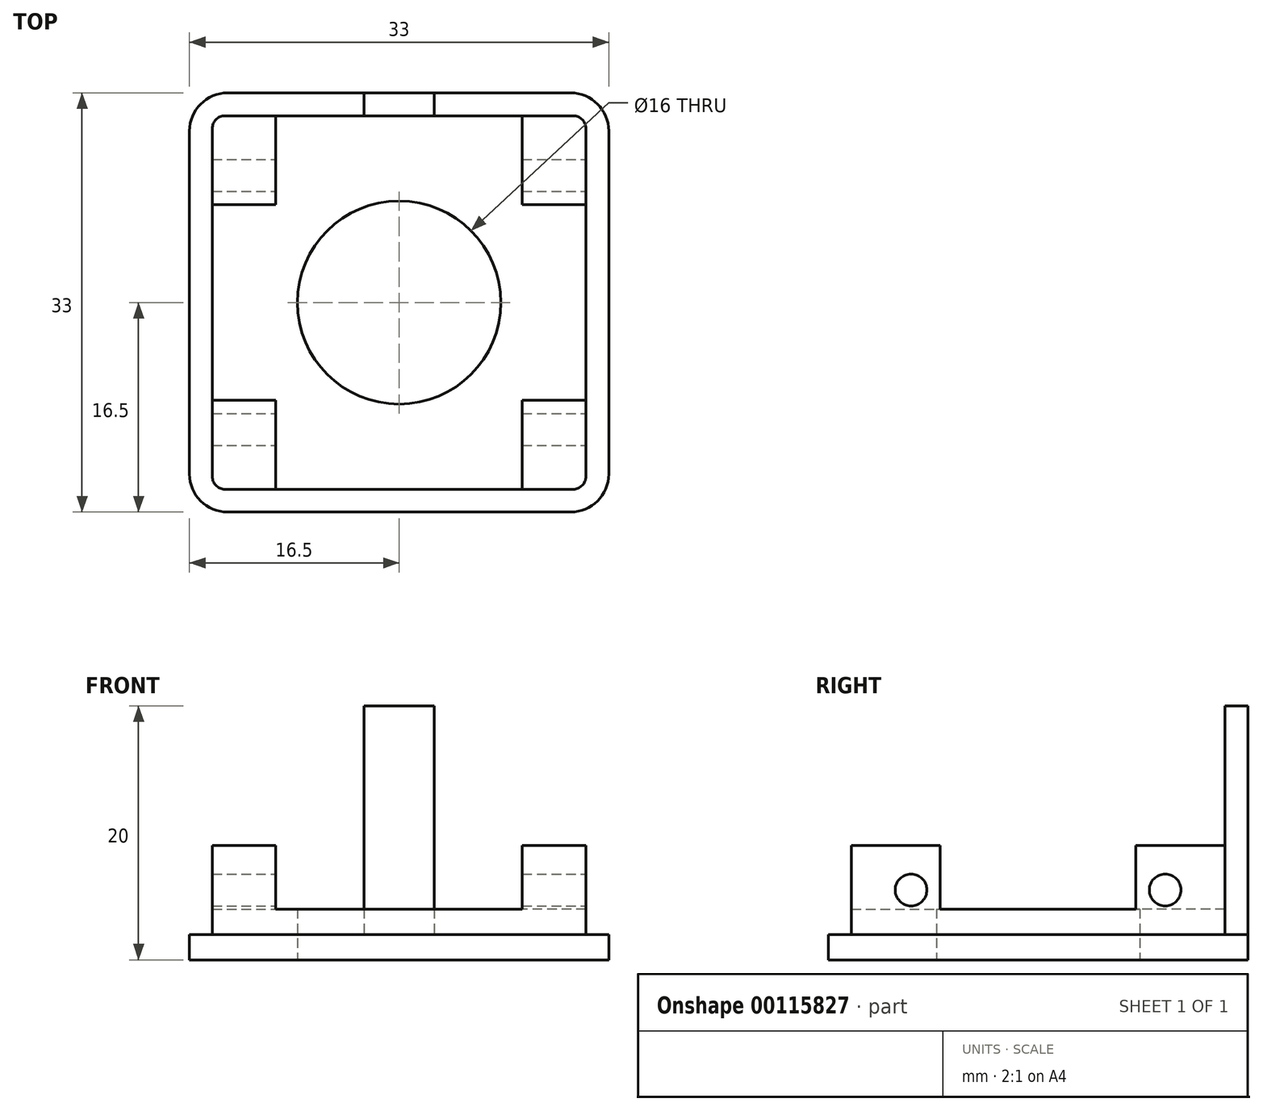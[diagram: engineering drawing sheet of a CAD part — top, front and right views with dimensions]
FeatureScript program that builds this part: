
annotation { "Feature Type Name" : "Feature", "Feature Type Description" : "" }
export const myFeature = defineFeature(function(context is Context, id is Id, definition is map)
    precondition{}
    {
        {
            var Q0;
            Q0=qCreatedBy(makeId("Top.planeOp"),FACE);
            var sketch = newSketch(context, id + "F0", { "sketchPlane" : qUnion([Q0])});
            skLineSegment(sketch, "E0.bottom", {"start": v(0, 0) * mm, "end": v(33, 0) * mm});
            skLineSegment(sketch, "E0.top", {"start": v(0, -33) * mm, "end": v(33, -33) * mm});
            skLineSegment(sketch, "E0.left", {"start": v(0, 0) * mm, "end": v(0, -33) * mm});
            skLineSegment(sketch, "E0.right", {"start": v(33, 0) * mm, "end": v(33, -33) * mm});
            skSolve(sketch);
        }
        {
            var Q0;
            Q0 = qSketchRegion(id + "F0", true);
            extrude(context, id + "F1", {"entities" : qUnion([Q0]), "depth" : 2 * mm});
        }
        {
            var Q0;
            Q0=makeQuery(id+"F1.opExtrude","CAP_FACE",FACE,{"disambiguationData":[OSD([sQuery(id+"F0.wireOp",EDGE,"E0.bottom"),sQuery(id+"F0.wireOp",EDGE,"E0.top"),sQuery(id+"F0.wireOp",EDGE,"E0.left"),sQuery(id+"F0.wireOp",EDGE,"E0.right")])],"isStart":false});
            var sketch = newSketch(context, id + "F2", { "sketchPlane" : qUnion([Q0])});
            skLineSegment(sketch, "E1.bottom", {"start": v(1.8, -1.8) * mm, "end": v(31.2, -1.8) * mm});
            skLineSegment(sketch, "E1.top", {"start": v(1.8, -31.2) * mm, "end": v(31.2, -31.2) * mm});
            skLineSegment(sketch, "E1.left", {"start": v(1.8, -1.8) * mm, "end": v(1.8, -31.2) * mm});
            skLineSegment(sketch, "E1.right", {"start": v(31.2, -1.8) * mm, "end": v(31.2, -31.2) * mm});
            skSolve(sketch);
        }
        {
            var Q0;
            Q0 = qSketchRegion(id + "F2", true);
            extrude(context, id + "F3", {"entities" : qUnion([Q0]), "operationType" : NewBodyOperationType.ADD, "depth" : 2 * mm});
        }
        {
            var Q0;
            Q0=makeQuery(id+"F3.opExtrude","CAP_FACE",FACE,{"disambiguationData":[OSD([sQuery(id+"F2.wireOp",EDGE,"E1.bottom"),sQuery(id+"F2.wireOp",EDGE,"E1.top"),sQuery(id+"F2.wireOp",EDGE,"E1.left"),sQuery(id+"F2.wireOp",EDGE,"E1.right")])],"isStart":false});
            var sketch = newSketch(context, id + "F4", { "sketchPlane" : qUnion([Q0])});
            skLineSegment(sketch, "E2.bottom", {"start": v(1.8, -1.8) * mm, "end": v(6.8, -1.8) * mm});
            skLineSegment(sketch, "E2.top", {"start": v(1.8, -8.8) * mm, "end": v(6.8, -8.8) * mm});
            skLineSegment(sketch, "E2.left", {"start": v(1.8, -1.8) * mm, "end": v(1.8, -8.8) * mm});
            skLineSegment(sketch, "E2.right", {"start": v(6.8, -1.8) * mm, "end": v(6.8, -8.8) * mm});
            skLineSegment(sketch, "E3.bottom", {"start": v(1.8, -31.2) * mm, "end": v(6.8, -31.2) * mm});
            skLineSegment(sketch, "E3.top", {"start": v(1.8, -24.2) * mm, "end": v(6.8, -24.2) * mm});
            skLineSegment(sketch, "E3.left", {"start": v(1.8, -31.2) * mm, "end": v(1.8, -24.2) * mm});
            skLineSegment(sketch, "E3.right", {"start": v(6.8, -31.2) * mm, "end": v(6.8, -24.2) * mm});
            skLineSegment(sketch, "E4.bottom", {"start": v(31.2, -1.8) * mm, "end": v(26.2, -1.8) * mm});
            skLineSegment(sketch, "E4.top", {"start": v(31.2, -8.8) * mm, "end": v(26.2, -8.8) * mm});
            skLineSegment(sketch, "E4.left", {"start": v(31.2, -1.8) * mm, "end": v(31.2, -8.8) * mm});
            skLineSegment(sketch, "E4.right", {"start": v(26.2, -1.8) * mm, "end": v(26.2, -8.8) * mm});
            skLineSegment(sketch, "E5.bottom", {"start": v(31.2, -31.2) * mm, "end": v(26.2, -31.2) * mm});
            skLineSegment(sketch, "E5.top", {"start": v(31.2, -24.2) * mm, "end": v(26.2, -24.2) * mm});
            skLineSegment(sketch, "E5.left", {"start": v(31.2, -31.2) * mm, "end": v(31.2, -24.2) * mm});
            skLineSegment(sketch, "E5.right", {"start": v(26.2, -31.2) * mm, "end": v(26.2, -24.2) * mm});
            skSolve(sketch);
        }
        {
            var Q0;
            Q0 = qSketchRegion(id + "F4", true);
            extrude(context, id + "F5", {"entities" : qUnion([Q0]), "operationType" : NewBodyOperationType.ADD, "depth" : 5 * mm});
        }
        {
            var Q0;
            Q0=makeQuery(id+"F1.opExtrude","CAP_FACE",FACE,{"disambiguationData":[OSD([sQuery(id+"F0.wireOp",EDGE,"E0.bottom"),sQuery(id+"F0.wireOp",EDGE,"E0.top"),sQuery(id+"F0.wireOp",EDGE,"E0.left"),sQuery(id+"F0.wireOp",EDGE,"E0.right")])],"isStart":true});
            var sketch = newSketch(context, id + "F6", { "sketchPlane" : qUnion([Q0])});
            skCircle(sketch, "E6", {"center": v(16.5, 16.5) * mm, "radius": 8 * mm});
            skSolve(sketch);
        }
        {
            var Q0;
            Q0 = qSketchRegion(id + "F6", true);
            extrude(context, id + "F7", {"entities" : qUnion([Q0]), "operationType" : NewBodyOperationType.REMOVE, "oppositeDirection" : true, "depth" : 25 * mm});
        }
        {
            var Q0;
            Q0=makeQuery(id+"F5.boolean.opBoolean","MERGE",FACE,{"derivedFrom":[makeQuery(id+"F3.opExtrude","SWEPT_FACE",FACE,{"disambiguationData":[OSD([sQuery(id+"F2.wireOp",EDGE,"E1.right")])]}),makeQuery(id+"F5.opExtrude","SWEPT_FACE",FACE,{"disambiguationData":[OSD([sQuery(id+"F4.wireOp",EDGE,"A4HpzIM3-QERc-0lZX-NRVA-JxbZbPFli9OZ.left")])]})]});
            var sketch = newSketch(context, id + "F8", { "sketchPlane" : qUnion([Q0])});
            skCircle(sketch, "E7", {"center": v(-26.5, 5.5) * mm, "radius": 1.25 * mm});
            skCircle(sketch, "E8", {"center": v(-6.5, 5.5) * mm, "radius": 1.25 * mm});
            skSolve(sketch);
        }
        {
            var Q0;
            Q0 = qSketchRegion(id + "F8", true);
            extrude(context, id + "F9", {"entities" : qUnion([Q0]), "operationType" : NewBodyOperationType.REMOVE, "oppositeDirection" : true, "depth" : 35 * mm});
        }
        {
            var Q0;
            Q0=makeQuery(id+"F5.boolean.opBoolean","MERGE",EDGE,{"derivedFrom":[makeQuery(id+"F3.opExtrude","SWEPT_EDGE",EDGE,{"disambiguationData":[OSD([sQuery(id+"F2.wireOp",EDGE,"E1.bottom"),sQuery(id+"F2.wireOp",EDGE,"E1.right")])]}),makeQuery(id+"F5.opExtrude","SWEPT_EDGE",EDGE,{"disambiguationData":[OSD([sQuery(id+"F4.wireOp",EDGE,"A4HpzIM3-QERc-0lZX-NRVA-JxbZbPFli9OZ.bottom"),sQuery(id+"F4.wireOp",EDGE,"A4HpzIM3-QERc-0lZX-NRVA-JxbZbPFli9OZ.left")])]})]});
            var Q1;
            Q1=makeQuery(id+"F5.boolean.opBoolean","MERGE",EDGE,{"derivedFrom":[makeQuery(id+"F3.opExtrude","SWEPT_EDGE",EDGE,{"disambiguationData":[OSD([sQuery(id+"F2.wireOp",EDGE,"E1.bottom"),sQuery(id+"F2.wireOp",EDGE,"E1.left")])]}),makeQuery(id+"F5.opExtrude","SWEPT_EDGE",EDGE,{"disambiguationData":[OSD([sQuery(id+"F4.wireOp",EDGE,"JeoF9uCe-VuEI-9JwQ-Yyk8-Sf0uGt0vNb40.bottom"),sQuery(id+"F4.wireOp",EDGE,"JeoF9uCe-VuEI-9JwQ-Yyk8-Sf0uGt0vNb40.left")])]})]});
            var Q2;
            Q2=makeQuery(id+"F5.boolean.opBoolean","MERGE",EDGE,{"derivedFrom":[makeQuery(id+"F3.opExtrude","SWEPT_EDGE",EDGE,{"disambiguationData":[OSD([sQuery(id+"F2.wireOp",EDGE,"E1.top"),sQuery(id+"F2.wireOp",EDGE,"E1.left")])]}),makeQuery(id+"F5.opExtrude","SWEPT_EDGE",EDGE,{"disambiguationData":[OSD([sQuery(id+"F4.wireOp",EDGE,"JeoF9uCe-VuEI-9JwQ-Yyk8-Sf0uGt0vNb40.top"),sQuery(id+"F4.wireOp",EDGE,"JeoF9uCe-VuEI-9JwQ-Yyk8-Sf0uGt0vNb40.left")])]})]});
            var Q3;
            Q3=makeQuery(id+"F5.boolean.opBoolean","MERGE",EDGE,{"derivedFrom":[makeQuery(id+"F3.opExtrude","SWEPT_EDGE",EDGE,{"disambiguationData":[OSD([sQuery(id+"F2.wireOp",EDGE,"E1.top"),sQuery(id+"F2.wireOp",EDGE,"E1.right")])]}),makeQuery(id+"F5.opExtrude","SWEPT_EDGE",EDGE,{"disambiguationData":[OSD([sQuery(id+"F4.wireOp",EDGE,"A4HpzIM3-QERc-0lZX-NRVA-JxbZbPFli9OZ.top"),sQuery(id+"F4.wireOp",EDGE,"A4HpzIM3-QERc-0lZX-NRVA-JxbZbPFli9OZ.left")])]})]});
            fillet(context, id + "F10", {"entities" : qUnion([Q0, Q1, Q2, Q3]), "radius" : 1 * mm, "tangentPropagation" : true, "allowEdgeOverflow" : false});
        }
        {
            var Q0;
            Q0=makeQuery(id+"F1.opExtrude","SWEPT_EDGE",EDGE,{"disambiguationData":[OSD([sQuery(id+"F0.wireOp",EDGE,"E0.top"),sQuery(id+"F0.wireOp",EDGE,"E0.left")])]});
            var Q1;
            Q1=makeQuery(id+"F1.opExtrude","SWEPT_EDGE",EDGE,{"disambiguationData":[OSD([sQuery(id+"F0.wireOp",EDGE,"E0.top"),sQuery(id+"F0.wireOp",EDGE,"E0.right")])]});
            var Q2;
            Q2=makeQuery(id+"F1.opExtrude","SWEPT_EDGE",EDGE,{"disambiguationData":[OSD([sQuery(id+"F0.wireOp",EDGE,"E0.bottom"),sQuery(id+"F0.wireOp",EDGE,"E0.left")])]});
            var Q3;
            Q3=makeQuery(id+"F1.opExtrude","SWEPT_EDGE",EDGE,{"disambiguationData":[OSD([sQuery(id+"F0.wireOp",EDGE,"E0.bottom"),sQuery(id+"F0.wireOp",EDGE,"E0.right")])]});
            fillet(context, id + "F11", {"entities" : qUnion([Q0, Q1, Q2, Q3]), "radius" : 3 * mm, "tangentPropagation" : true, "allowEdgeOverflow" : false});
        }
        {
            var Q0;
            Q0=makeQuery(id+"F1.opExtrude","CAP_FACE",FACE,{"disambiguationData":[OSD([sQuery(id+"F0.wireOp",EDGE,"E0.bottom"),sQuery(id+"F0.wireOp",EDGE,"E0.top"),sQuery(id+"F0.wireOp",EDGE,"E0.left"),sQuery(id+"F0.wireOp",EDGE,"E0.right")])],"isStart":false});
            var sketch = newSketch(context, id + "F12", { "sketchPlane" : qUnion([Q0])});
            skLineSegment(sketch, "E9.bottom", {"start": v(19.25, -1.8) * mm, "end": v(13.75, -1.8) * mm});
            skLineSegment(sketch, "E9.top", {"start": v(19.25, 0) * mm, "end": v(13.75, 0) * mm});
            skLineSegment(sketch, "E9.left", {"start": v(19.25, -1.8) * mm, "end": v(19.25, 0) * mm});
            skLineSegment(sketch, "E9.right", {"start": v(13.75, -1.8) * mm, "end": v(13.75, 0) * mm});
            skPoint(sketch, "E10", {"position": v(16.5, 0) * mm});
            skSolve(sketch);
        }
        {
            var Q0;
            Q0 = qSketchRegion(id + "F12", true);
            extrude(context, id + "F13", {"entities" : qUnion([Q0]), "operationType" : NewBodyOperationType.ADD, "depth" : 18 * mm});
        }
    });
